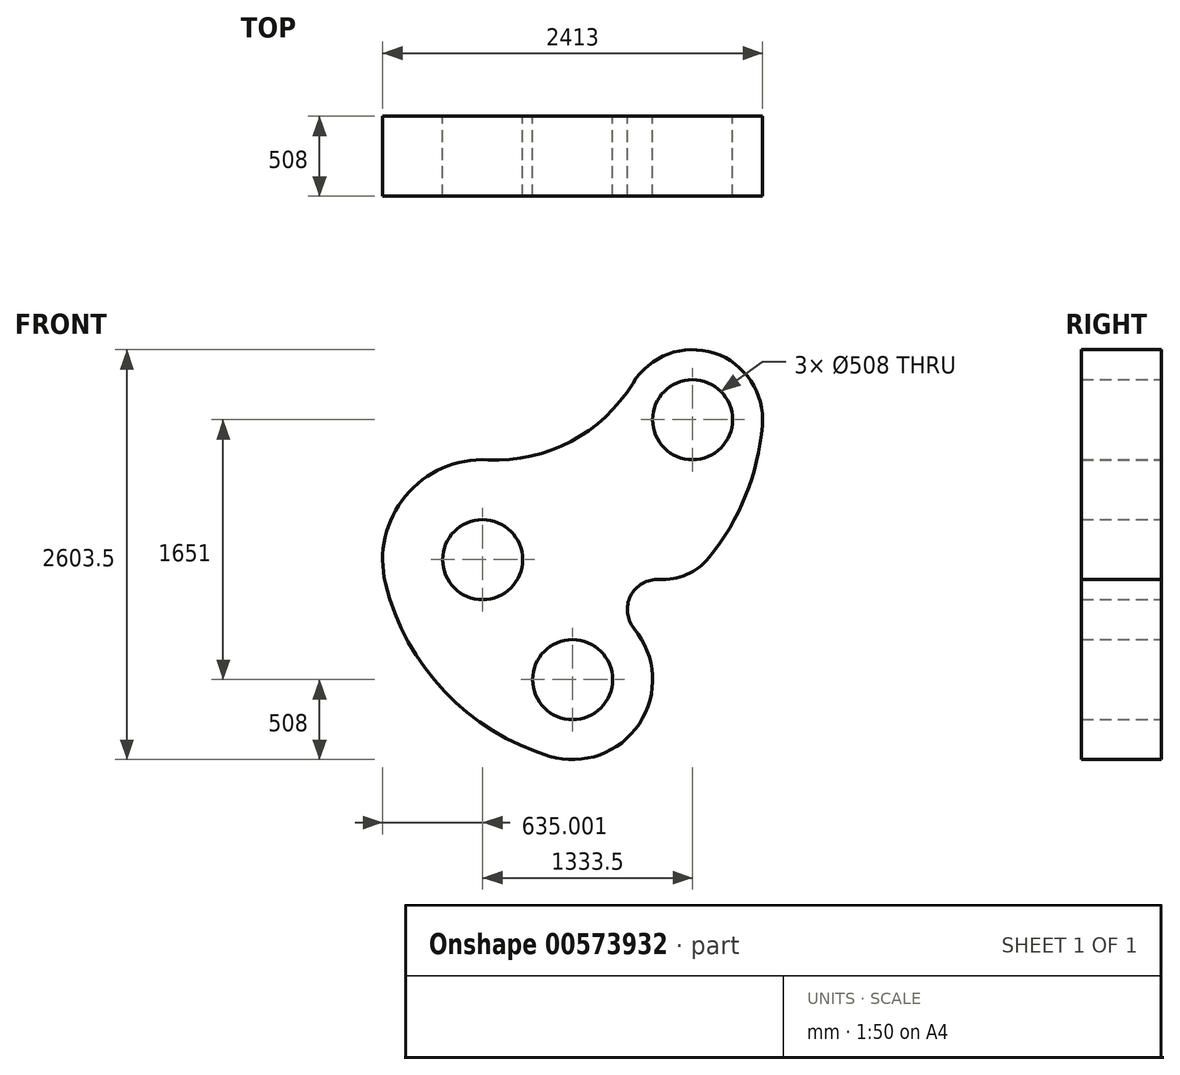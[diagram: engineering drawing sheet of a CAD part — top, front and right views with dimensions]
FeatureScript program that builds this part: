
annotation { "Feature Type Name" : "Feature", "Feature Type Description" : "" }
export const myFeature = defineFeature(function(context is Context, id is Id, definition is map)
    precondition{}
    {
        {
            var Q0;
            Q0=qCreatedBy(makeId("Front.planeOp"),FACE);
            var sketch = newSketch(context, id + "F0", { "sketchPlane" : qUnion([Q0])});
            skArc(sketch, "E0", {"start": v(1513.8, 380.13) * mm, "mid": v(991.58, 151) * mm, "end": v(863.83, -404.8) * mm});
            skArc(sketch, "E1", {"start": v(1906.13, -1502.56) * mm, "mid": v(2475.58, -1296.68) * mm, "end": v(2443.44, -692.01) * mm});
            skCircle(sketch, "E2", {"center": v(2814.16, 635) * mm, "radius": 254 * mm});
            skArc(sketch, "E3", {"start": v(3257.19, 598.84) * mm, "mid": v(2951.56, 1057.73) * mm, "end": v(2434.54, 866.23) * mm});
            skCircle(sketch, "E4", {"center": v(1480.66, -254) * mm, "radius": 254 * mm});
            skCircle(sketch, "E5", {"center": v(2052.16, -1016) * mm, "radius": 254 * mm});
            skArc(sketch, "E6", {"start": v(863.83, -404.8) * mm, "mid": v(1239.04, -1092.24) * mm, "end": v(1906.13, -1502.56) * mm});
            skArc(sketch, "E7", {"start": v(2601.33, -380.35) * mm, "mid": v(2776.84, -348.85) * mm, "end": v(2918.8, -240.94) * mm});
            skArc(sketch, "E8", {"start": v(2918.8, -240.94) * mm, "mid": v(3151.8, 153.24) * mm, "end": v(3257.19, 598.84) * mm});
            skArc(sketch, "E9", {"start": v(2601.33, -380.35) * mm, "mid": v(2420.23, -484.43) * mm, "end": v(2443.44, -692.01) * mm});
            skArc(sketch, "E10", {"start": v(1513.8, 380.13) * mm, "mid": v(2041.17, 496.28) * mm, "end": v(2434.54, 866.23) * mm});
            skSolve(sketch);
        }
        {
            var Q0;
            Q0=makeQuery(id+"F0.imprint","IMPRINT",FACE,{"disambiguationData":[TD([[makeQuery(id+"F0.imprint","IMPRINT",EDGE,{"derivedFrom":sQuery(id+"F0.wireOp",EDGE,"E0")}),1.0]])]});
            extrude(context, id + "F1", {"entities" : qUnion([Q0]), "depth" : 508 * mm, "offsetDistance" : 25.4 * mm});
        }
    });
